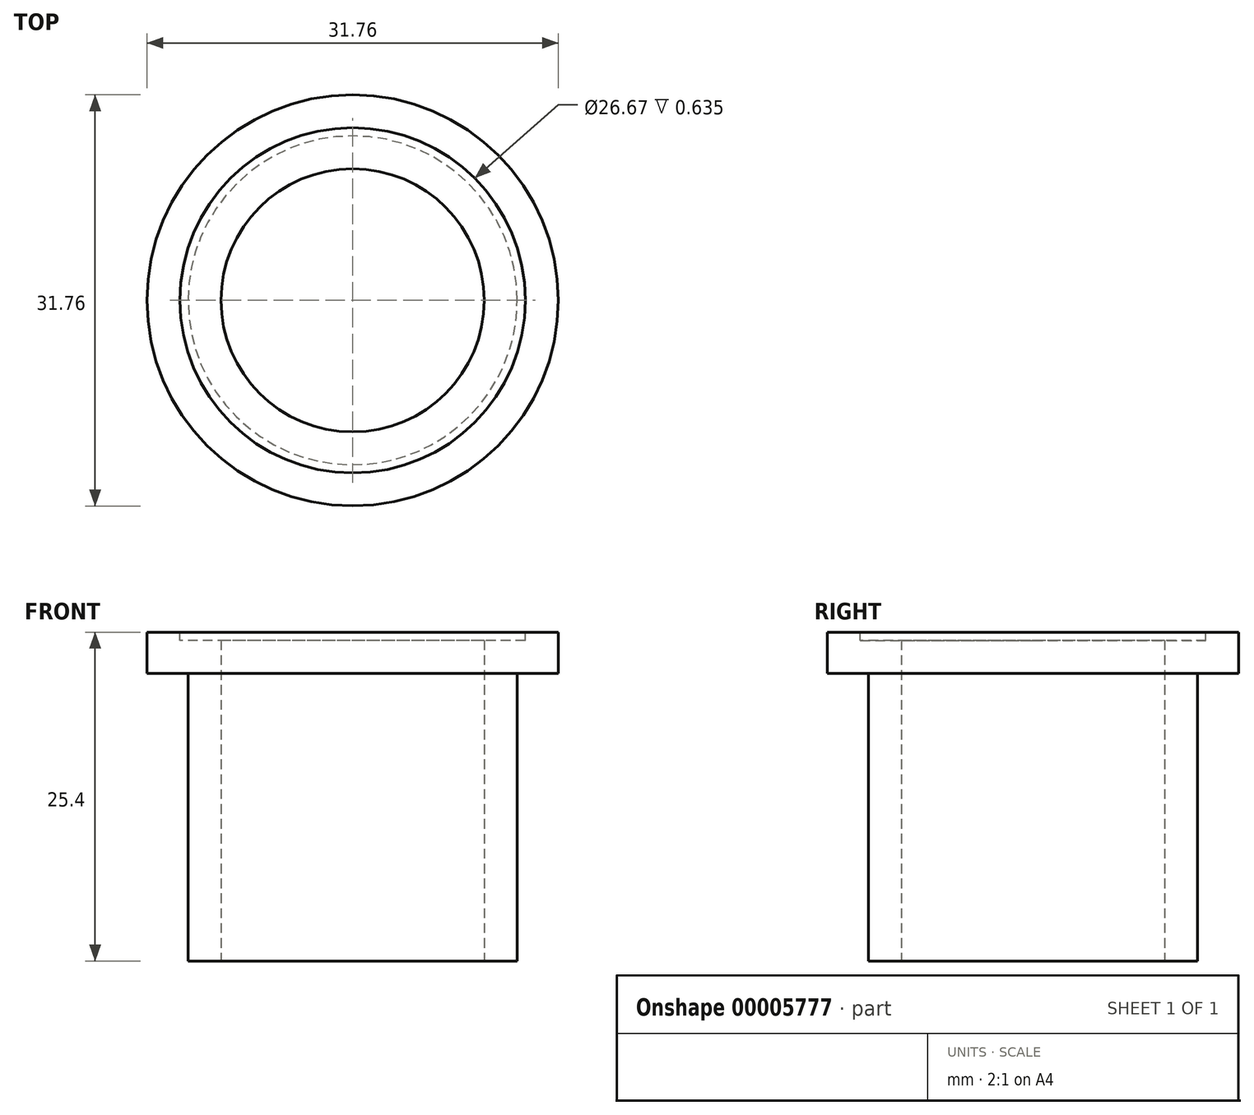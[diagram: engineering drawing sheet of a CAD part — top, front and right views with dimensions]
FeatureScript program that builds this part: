
annotation { "Feature Type Name" : "Feature", "Feature Type Description" : "" }
export const myFeature = defineFeature(function(context is Context, id is Id, definition is map)
    precondition{}
    {
        {
            var Q0;
            Q0=qCreatedBy(makeId("Top.planeOp"),FACE);
            var sketch = newSketch(context, id + "F0", { "sketchPlane" : qUnion([Q0])});
            skCircle(sketch, "E0", {"center": v(0, 0) * mm, "radius": 12.7 * mm});
            skSolve(sketch);
        }
        {
            var Q0;
            Q0=makeQuery(id+"F0.imprint","IMPRINT",FACE,{"disambiguationData":[TD([[makeQuery(id+"F0.imprint","IMPRINT",EDGE,{"derivedFrom":sQuery(id+"F0.wireOp",EDGE,"E0")}),1.0]])]});
            extrude(context, id + "F1", {"entities" : qUnion([Q0]), "depth" : 25.4 * mm});
        }
        {
            var Q0;
            Q0=makeQuery(id+"F1.opExtrude","CAP_FACE",FACE,{"disambiguationData":[OSD([sQuery(id+"F0.wireOp",EDGE,"E0")])],"isStart":false});
            var sketch = newSketch(context, id + "F2", { "sketchPlane" : qUnion([Q0])});
            skCircle(sketch, "E1", {"center": v(0, 0) * mm, "radius": 15.88 * mm});
            skSolve(sketch);
        }
        {
            var Q0;
            Q0=makeQuery(id+"F2.imprint","IMPRINT",FACE,{"disambiguationData":[TD([[makeQuery(id+"F2.imprint","IMPRINT",EDGE,{"derivedFrom":sQuery(id+"F2.wireOp",EDGE,"E1")}),1.0]])]});
            extrude(context, id + "F3", {"entities" : qUnion([Q0]), "operationType" : NewBodyOperationType.ADD, "oppositeDirection" : true, "depth" : 3.17 * mm});
        }
        {
            var Q0;
            {var subQ0=sQuery(id+"F0.wireOp",EDGE,"E0");Q0=makeQuery(id+"F3.boolean.opBoolean","MERGE",FACE,{"derivedFrom":[makeQuery(id+"F1.opExtrude","CAP_FACE",FACE,{"disambiguationData":[OSD([subQ0])],"isStart":false}),makeQuery(id+"F3.opExtrude","CAP_FACE",FACE,{"disambiguationData":[OSD([subQ0,sQuery(id+"F2.wireOp",EDGE,"E1")])],"isStart":true})]});}
            var Q1;
            Q1=makeQuery(id+"F1.opExtrude","CAP_FACE",FACE,{"disambiguationData":[OSD([sQuery(id+"F0.wireOp",EDGE,"E0")])],"isStart":true});
            shell(context, id + "F4", {"entities" : qUnion([Q0, Q1]), "thickness" : 2.54 * mm});
        }
    });
